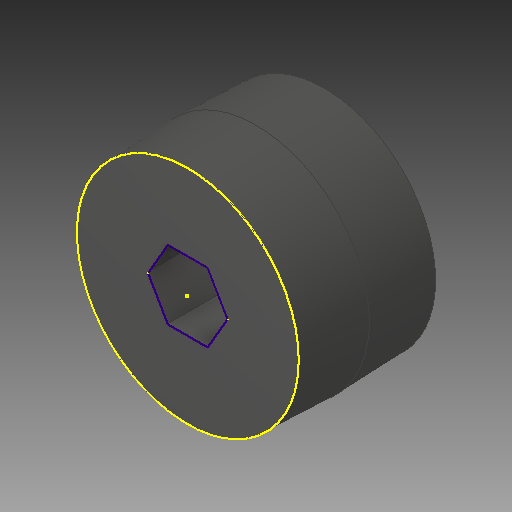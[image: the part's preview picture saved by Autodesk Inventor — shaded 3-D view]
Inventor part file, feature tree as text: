
AUTODESK INVENTOR PART (.ipt)
format: ipt  version: 2017 (Build 210142000, 142)  size: 685,568 bytes
history: native  units: in
note: dims shown in document units (in); Inventor stores cm internally (conversion verified against a paired STEP export)
features: sketch x1, projected_geometry x1, other x1
ambient origin geometry x8: Origin, YZ Plane, XZ Plane, XY Plane, X Axis, Y Axis, Z Axis, Center Point
bodies: Solid1 (feature_tree)
feature tree (3):
  sketch  "Sketch1"
  projected_geometry  "Projected Loop1"
  other  "_2in Wheel Intergrated Hub Design_-_CirPattern1_"
